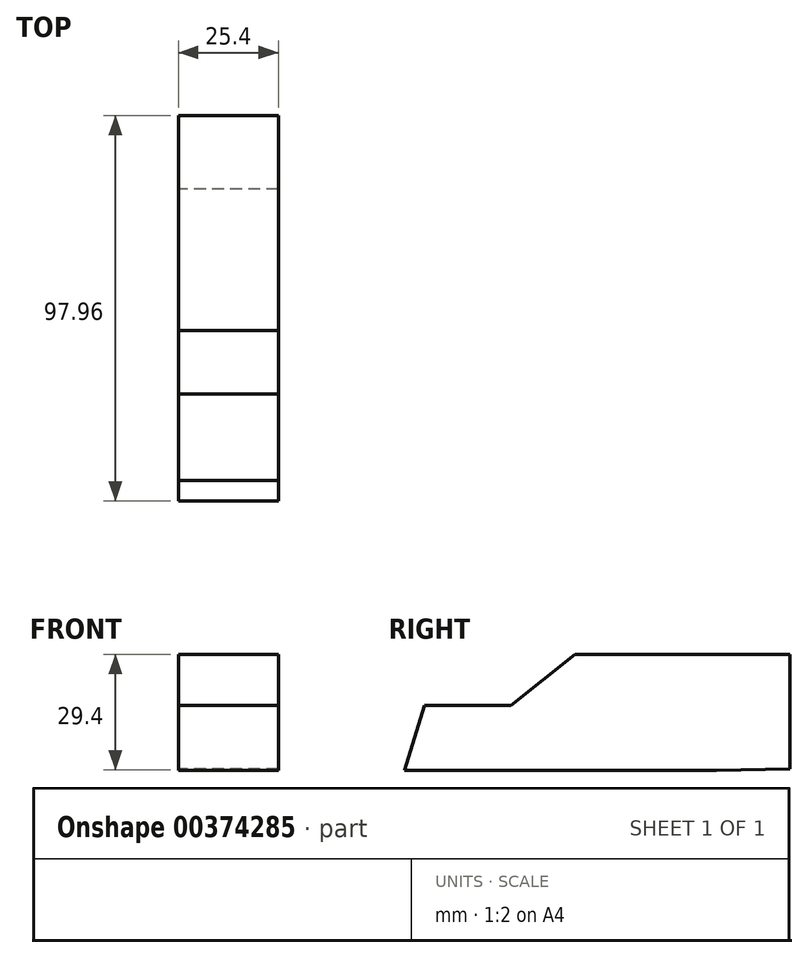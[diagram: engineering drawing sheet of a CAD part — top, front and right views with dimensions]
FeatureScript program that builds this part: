
annotation { "Feature Type Name" : "Feature", "Feature Type Description" : "" }
export const myFeature = defineFeature(function(context is Context, id is Id, definition is map)
    precondition{}
    {
        {
            var Q0;
            Q0=qCreatedBy(makeId("Right.planeOp"),FACE);
            var sketch = newSketch(context, id + "F0", { "sketchPlane" : qUnion([Q0])});
            skLineSegment(sketch, "E0", {"start": v(-38.2, 0) * mm, "end": v(-16.23, 0) * mm});
            skLineSegment(sketch, "E1", {"start": v(-16.23, 0) * mm, "end": v(0, 12.98) * mm});
            skLineSegment(sketch, "E2", {"start": v(0, 12.98) * mm, "end": v(35.9, 12.98) * mm});
            skLineSegment(sketch, "E3", {"start": v(35.9, -16.42) * mm, "end": v(-43.35, -16.42) * mm});
            skLineSegment(sketch, "E4", {"start": v(-43.35, -16.42) * mm, "end": v(-38.2, 0) * mm});
            skLineSegment(sketch, "E5", {"start": v(35.9, 12.98) * mm, "end": v(54.61, 12.98) * mm});
            skLineSegment(sketch, "E6", {"start": v(54.61, 12.98) * mm, "end": v(54.61, -16.04) * mm});
            skLineSegment(sketch, "E7", {"start": v(54.61, -16.04) * mm, "end": v(35.9, -16.42) * mm});
            skSolve(sketch);
        }
        {
            var Q0;
            Q0=makeQuery(id+"F0.imprint","IMPRINT",FACE,{"disambiguationData":[TD([[makeQuery(id+"F0.imprint","IMPRINT",EDGE,{"derivedFrom":sQuery(id+"F0.wireOp",EDGE,"E0")}),-1.0]])]});
            var Q1;
            Q1=makeQuery(id+"F0.imprint","IMPRINT",FACE,{"disambiguationData":[TD([[makeQuery(id+"F0.imprint","IMPRINT",EDGE,{"derivedFrom":sQuery(id+"F0.wireOp",EDGE,"i36Eh6km-GE1U-6eUF-rptL-GrnXEwg31PMt")}),1.0]])]});
            extrude(context, id + "F1", {"entities" : qUnion([Q0, Q1]), "depth" : 25.4 * mm});
        }
    });
